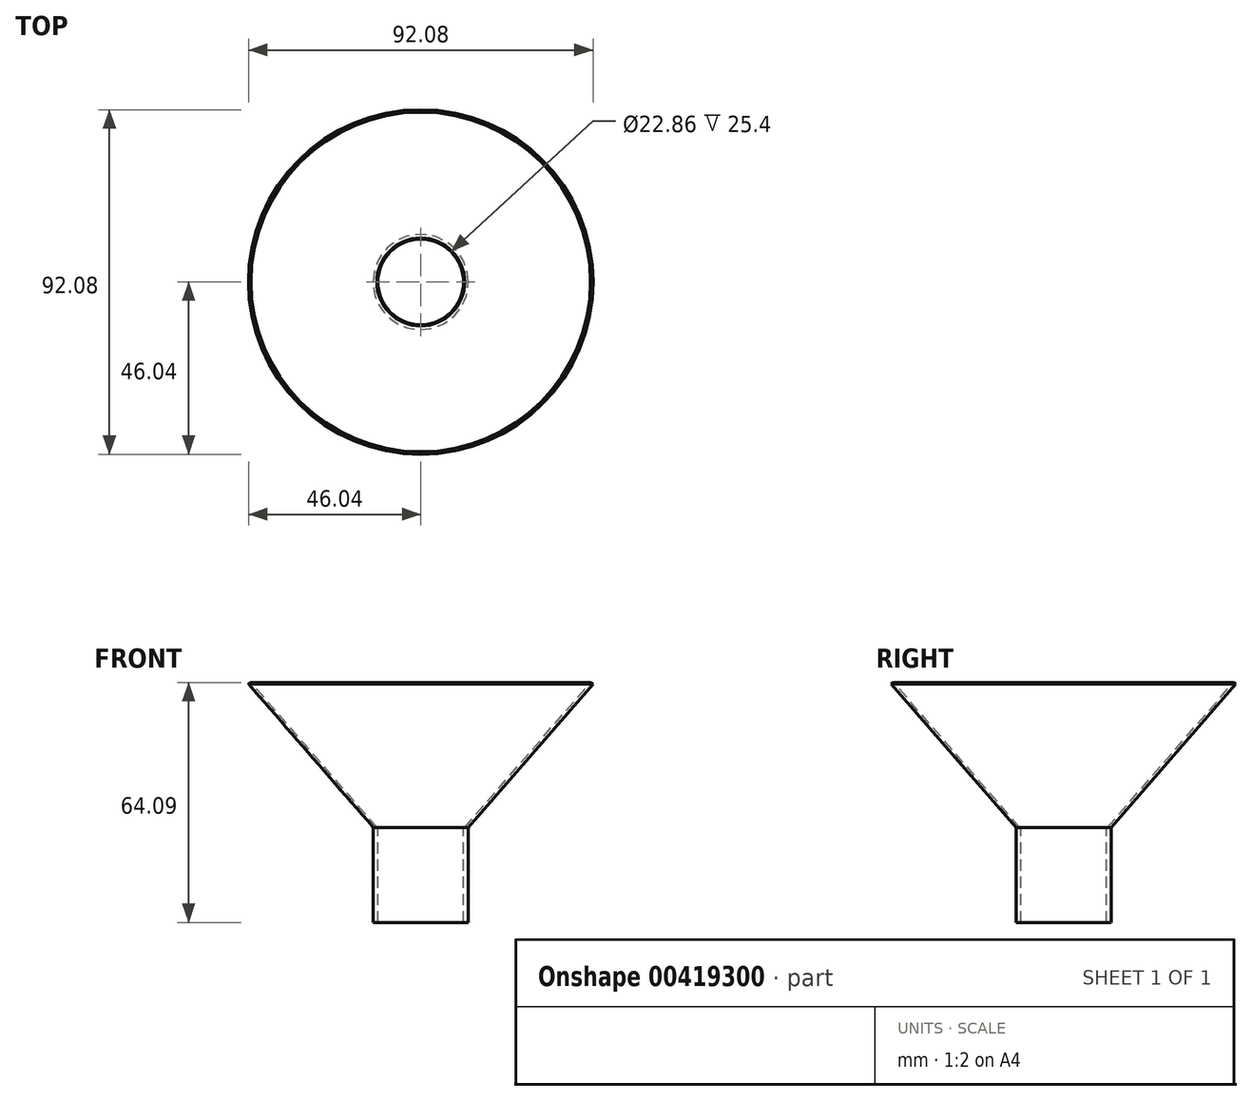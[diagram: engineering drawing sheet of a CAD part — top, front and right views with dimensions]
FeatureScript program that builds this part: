
annotation { "Feature Type Name" : "Feature", "Feature Type Description" : "" }
export const myFeature = defineFeature(function(context is Context, id is Id, definition is map)
    precondition{}
    {
        {
            var Q0;
            Q0=qCreatedBy(makeId("Front.planeOp"),FACE);
            var sketch = newSketch(context, id + "F0", { "sketchPlane" : qUnion([Q0])});
            skLineSegment(sketch, "E0", {"start": v(0, 0) * mm, "end": v(33.34, 38.33) * mm});
            skLineSegment(sketch, "E1", {"start": v(0, 0) * mm, "end": v(0, -25.4) * mm});
            skLineSegment(sketch, "E2", {"start": v(0, -25.4) * mm, "end": v(-12.7, -25.4) * mm});
            skLineSegment(sketch, "E3", {"start": v(-12.7, -25.4) * mm, "end": v(-12.7, 0) * mm});
            skLineSegment(sketch, "E4", {"start": v(-12.7, 0) * mm, "end": v(-0.95, 0) * mm});
            skLineSegment(sketch, "E5", {"start": v(-0.95, 0) * mm, "end": v(32.7, 38.69) * mm});
            skLineSegment(sketch, "E6", {"start": v(32.7, 38.69) * mm, "end": v(33.34, 38.33) * mm});
            skSolve(sketch);
        }
        {
            var Q0;
            Q0=makeQuery(id+"F0.imprint","IMPRINT",FACE,{"disambiguationData":[TD([[makeQuery(id+"F0.imprint","IMPRINT",EDGE,{"derivedFrom":sQuery(id+"F0.wireOp",EDGE,"E0")}),1.0]])]});
            var Q1;
            Q1=sQuery(id+"F0.wireOp",EDGE,"E4");
            var Q2;
            Q2=sQuery(id+"F0.wireOp",EDGE,"E3");
            revolve(context, id + "F1", {"entities" : qUnion([Q0]), "surfaceEntities" : qUnion([Q1]), "axis" : qUnion([Q2]), "revolveType" : RevolveType.FULL});
        }
        {
            var Q0;
            Q0=qCreatedBy(makeId("Top.planeOp"),FACE);
            var sketch = newSketch(context, id + "F2", { "sketchPlane" : qUnion([Q0])});
            skCircle(sketch, "E7", {"center": v(-12.7, 0) * mm, "radius": 11.43 * mm});
            skSolve(sketch);
        }
        {
            var Q0;
            Q0 = qSketchRegion(id + "F2", true);
            extrude(context, id + "F3", {"entities" : qUnion([Q0]), "operationType" : NewBodyOperationType.REMOVE, "oppositeDirection" : true, "depth" : 25.4 * mm});
        }
    });
